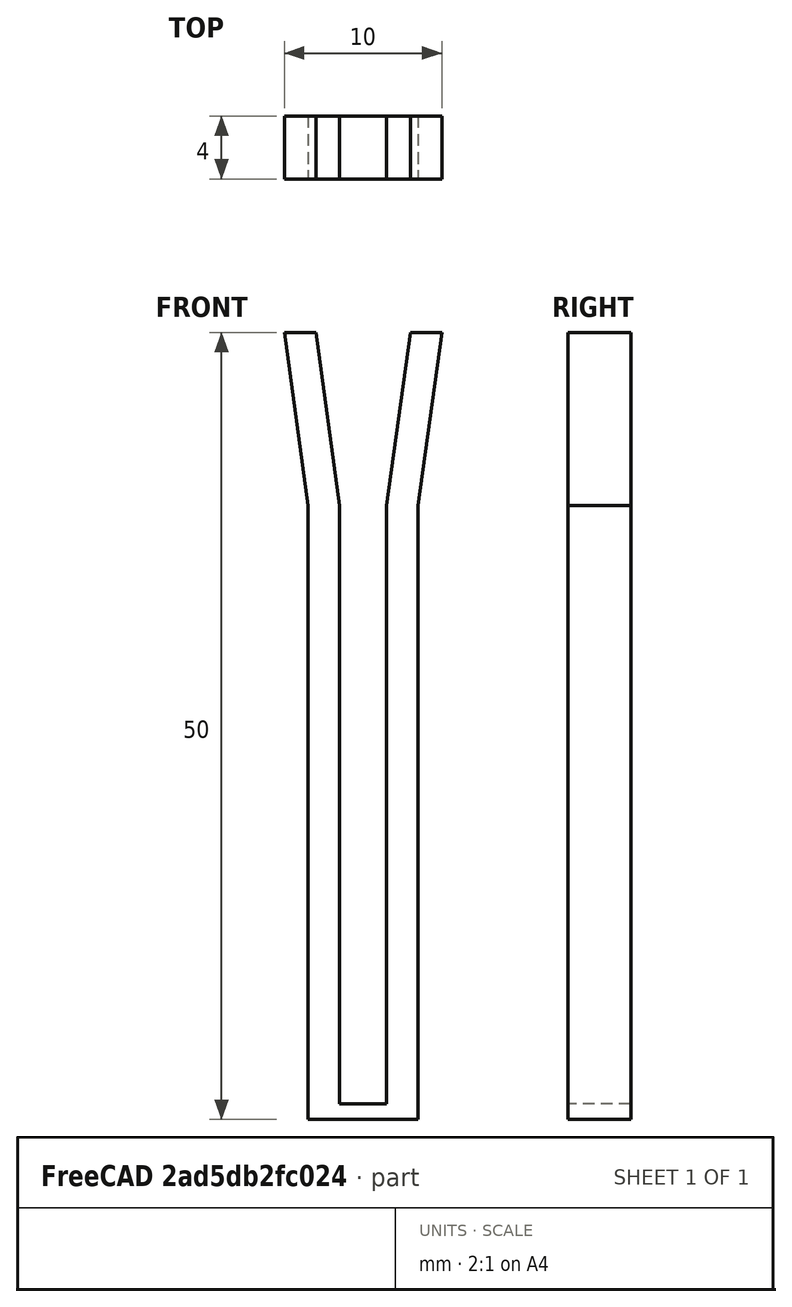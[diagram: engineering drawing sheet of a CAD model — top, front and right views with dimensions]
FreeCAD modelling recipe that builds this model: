
FCSTD DOCUMENT  (FreeCAD 0.16R6712 (Git))
Label: Guide Vee (Deeper)
License: All rights reserved
LicenseURL: http://en.wikipedia.org/wiki/All_rights_reserved
objects: Sketcher::SketchObject×1, PartDesign::Pad×1
note: 3 computed .brp shape members not serialized (recipe doc carries the construction recipe); baked Part::Feature solids carry a one-line shape summary decoded from their .brp

FEATURE [Sketcher::SketchObject] Sketch  label="Vee Support"
  Placement = pos=(0,0,0) rot=(1,0,0;1.5708rad)
  sketch-geometry (13):
    g0: LineSegment StartX=3 StartY=49 StartZ=0 EndX=1.5 EndY=38 EndZ=0
    g1: LineSegment StartX=1.5 StartY=38 StartZ=0 EndX=1.5 EndY=0 EndZ=0
    g2: LineSegment StartX=1.5 StartY=0 StartZ=0 EndX=-1.5 EndY=0 EndZ=0
    g3: LineSegment StartX=-1.5 StartY=0 StartZ=0 EndX=-1.5 EndY=38 EndZ=0
    g4: LineSegment StartX=-1.5 StartY=38 StartZ=0 EndX=-3 EndY=49 EndZ=0
    g5: LineSegment StartX=-3 StartY=49 StartZ=0 EndX=-5 EndY=49 EndZ=0
    g6: LineSegment StartX=-5 StartY=49 StartZ=0 EndX=-3.5 EndY=38 EndZ=0
    g7: LineSegment StartX=-3.5 StartY=38 StartZ=0 EndX=-3.5 EndY=-1 EndZ=0
    g8: LineSegment StartX=-3.5 StartY=-1 StartZ=0 EndX=3.5 EndY=-1 EndZ=0
    g9: LineSegment StartX=3.5 StartY=-1 StartZ=0 EndX=3.5 EndY=38 EndZ=0
    g10: LineSegment StartX=3.5 StartY=38 StartZ=0 EndX=5 EndY=49 EndZ=0
    g11: LineSegment StartX=5 StartY=49 StartZ=0 EndX=3 EndY=49 EndZ=0
    g12: LineSegment [constr] StartX=-3.5 StartY=38 StartZ=0 EndX=-1.5 EndY=38 EndZ=0
  constraints (35):
    c: Coincident(g0,g1)
    c: Coincident(g1,g2)
    c: Coincident(g2,g3)
    c: Coincident(g3,g4)
    c: Coincident(g4,g5)
    c: Coincident(g5,g6)
    c: Coincident(g6,g7)
    c: Coincident(g7,g8)
    c: Coincident(g8,g9)
    c: Coincident(g9,g10)
    c: Coincident(g10,g11)
    c: Coincident(g11,g0)
    c: Horizontal(g11)
    c: Horizontal(g5)
    c: Horizontal(g2)
    c: Horizontal(g8)
    c: Vertical(g3)
    c: Vertical(g1)
    c: Vertical(g9)
    c: Parallel(g6,g4)
    c: Parallel(g0,g10)
    c: Symmetric(g3,g0,g-2)
    c: Symmetric(g4,g0,g-2)
    c: DistanceX(g2) = -3
    c: DistanceX(g2,g7) = -2
    c: Symmetric(g7,g8,g-2)
    c: Symmetric(g6,g9,g-2)
    c: Horizontal(g12)
    c: Coincident(g6,g12)
    c: Coincident(g12,g3)
    c: DistanceY(g2,g7) = -1
    c: DistanceY(g5,g7) = -50
    c: DistanceY(g3,g2) = -38
    c: DistanceX(g4,g0) = 6
    c: PointOnObject(g2,g-1)
FEATURE [PartDesign::Pad] Pad
  Length = 4
  Length2 = 100
  Placement = pos=(0,0,0) rot=(1,0,0;1.5708rad)
  Sketch = -> Sketch
  Type = 0
